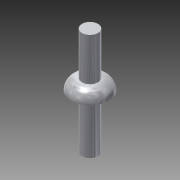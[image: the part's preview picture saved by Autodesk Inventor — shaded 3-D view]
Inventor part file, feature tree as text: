
AUTODESK INVENTOR PART (.ipt)
format: ipt  version: 2015 (Build 190159000, 159)  size: 90,624 bytes
history: native  units: mm
features: extrude x2, sketch x1, fillet x1
ambient origin geometry x8: Origin, YZ Plane, XZ Plane, XY Plane, X Axis, Y Axis, Z Axis, Center Point
bodies: Solid1 (feature_tree)
feature tree (4):
  sketch  "Sketch1"  dims[d0=1.5mm d1=3.5mm d2=10.0mm d3=0.0mm d4=1.0mm d5=0.0mm d6=1.0mm]
  extrude  "Extrusion1"  Depth=1.0mm
  extrude  "Extrusion2"  Depth=10.0mm TaperAngle=0.0deg
  fillet  "Fillet1"  Radius=1.0mm
